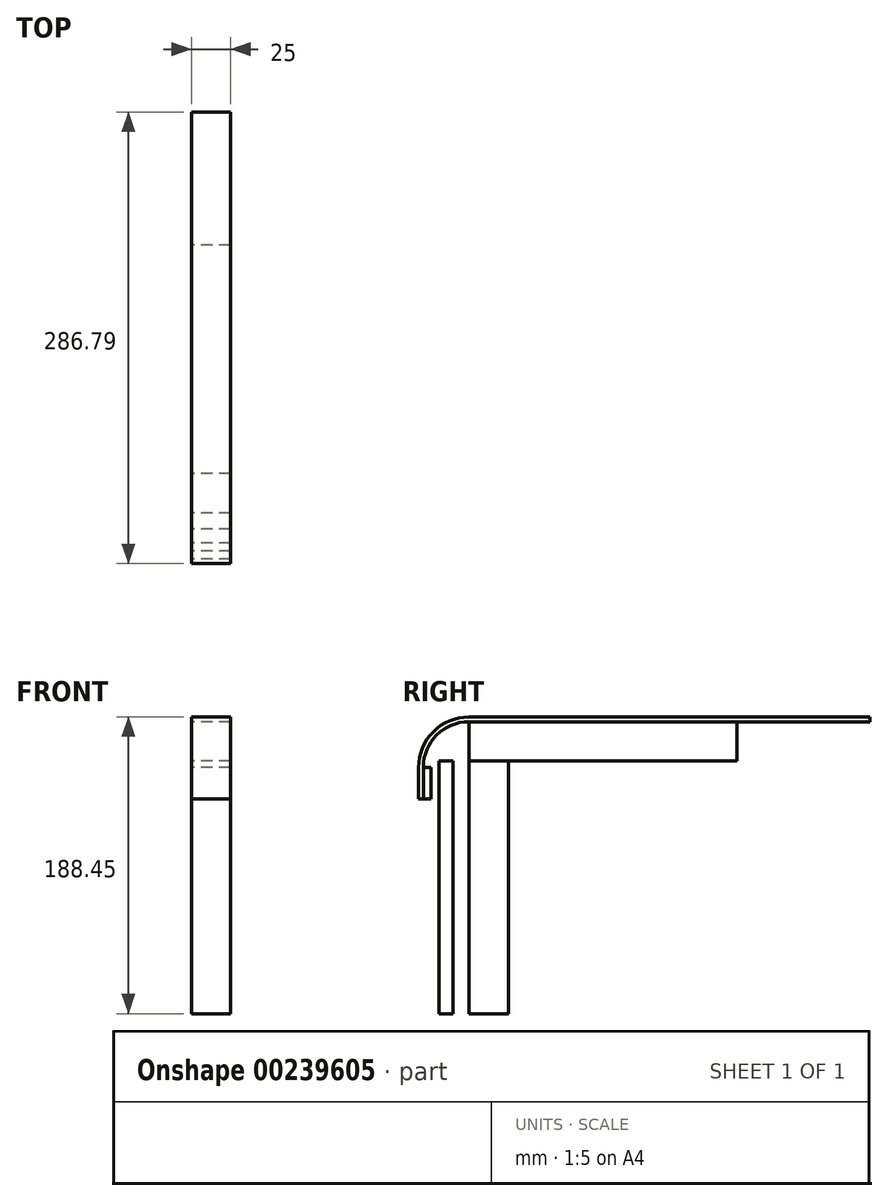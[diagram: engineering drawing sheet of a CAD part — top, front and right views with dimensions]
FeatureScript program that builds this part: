
annotation { "Feature Type Name" : "Feature", "Feature Type Description" : "" }
export const myFeature = defineFeature(function(context is Context, id is Id, definition is map)
    precondition{}
    {
        {
            var Q0;
            Q0=qCreatedBy(makeId("Right.planeOp"),FACE);
            var sketch = newSketch(context, id + "F0", { "sketchPlane" : qUnion([Q0])});
            skLineSegment(sketch, "E0.bottom", {"start": v(0, 0) * mm, "end": v(25, 0) * mm});
            skLineSegment(sketch, "E0.top", {"start": v(0, 160.45) * mm, "end": v(25, 160.45) * mm});
            skLineSegment(sketch, "E0.left", {"start": v(0, 0) * mm, "end": v(0, 160.45) * mm});
            skLineSegment(sketch, "E0.right", {"start": v(25, 0) * mm, "end": v(25, 160.45) * mm});
            skLineSegment(sketch, "E1.bottom", {"start": v(0, 160.45) * mm, "end": v(170.13, 160.45) * mm});
            skLineSegment(sketch, "E1.top", {"start": v(0, 185.45) * mm, "end": v(170.13, 185.45) * mm});
            skLineSegment(sketch, "E1.left", {"start": v(0, 160.45) * mm, "end": v(0, 185.45) * mm});
            skLineSegment(sketch, "E1.right", {"start": v(170.13, 160.45) * mm, "end": v(170.13, 185.45) * mm});
            skLineSegment(sketch, "E2", {"start": v(254.8, 188.45) * mm, "end": v(0, 188.45) * mm});
            skLineSegment(sketch, "E3.bottom", {"start": v(-10, 160.45) * mm, "end": v(-19, 160.45) * mm});
            skLineSegment(sketch, "E3.top", {"start": v(-10, 0) * mm, "end": v(-19, 0) * mm});
            skLineSegment(sketch, "E3.left", {"start": v(-10, 160.45) * mm, "end": v(-10, 0) * mm});
            skLineSegment(sketch, "E3.right", {"start": v(-19, 160.45) * mm, "end": v(-19, 0) * mm});
            skLineSegment(sketch, "E4.bottom", {"start": v(-29, 156.45) * mm, "end": v(-24, 156.45) * mm});
            skLineSegment(sketch, "E4.top", {"start": v(-29, 136.45) * mm, "end": v(-24, 136.45) * mm});
            skLineSegment(sketch, "E4.left", {"start": v(-29, 156.45) * mm, "end": v(-29, 136.45) * mm});
            skLineSegment(sketch, "E4.right", {"start": v(-24, 156.45) * mm, "end": v(-24, 136.45) * mm});
            skArc(sketch, "E5", {"start": v(0, 185.45) * mm, "mid": v(-20.5, 176.96) * mm, "end": v(-29, 156.45) * mm});
            skArc(sketch, "E6", {"start": v(0, 188.45) * mm, "mid": v(-22.63, 179.08) * mm, "end": v(-32, 156.45) * mm});
            skLineSegment(sketch, "E7", {"start": v(-32, 156.45) * mm, "end": v(-32, 136.45) * mm});
            skLineSegment(sketch, "E8", {"start": v(-32, 136.45) * mm, "end": v(-29, 136.45) * mm});
            skLineSegment(sketch, "E9", {"start": v(170.13, 185.45) * mm, "end": v(254.8, 185.45) * mm});
            skLineSegment(sketch, "E10", {"start": v(254.8, 185.45) * mm, "end": v(254.8, 188.45) * mm});
            skSolve(sketch);
        }
        {
            var Q0;
            Q0=makeQuery(id+"F0.imprint","IMPRINT",FACE,{"disambiguationData":[TD([[makeQuery(id+"F0.imprint","IMPRINT",EDGE,{"derivedFrom":sQuery(id+"F0.wireOp",EDGE,"E1.top")}),1.0]])]});
            extrude(context, id + "F1", {"entities" : qUnion([Q0]), "depth" : 25 * mm});
        }
        {
            var Q0;
            Q0=makeQuery(id+"F0.imprint","IMPRINT",FACE,{"disambiguationData":[TD([[makeQuery(id+"F0.imprint","IMPRINT",EDGE,{"derivedFrom":sQuery(id+"F0.wireOp",EDGE,"E1.top")}),-1.0]])]});
            extrude(context, id + "F2", {"entities" : qUnion([Q0]), "depth" : 25 * mm});
        }
        {
            var Q0;
            Q0=makeQuery(id+"F0.imprint","IMPRINT",FACE,{"disambiguationData":[TD([[makeQuery(id+"F0.imprint","IMPRINT",EDGE,{"derivedFrom":sQuery(id+"F0.wireOp",EDGE,"E0.bottom")}),1.0]])]});
            extrude(context, id + "F3", {"entities" : qUnion([Q0]), "depth" : 25 * mm});
        }
        {
            var Q0;
            Q0=makeQuery(id+"F0.imprint","IMPRINT",FACE,{"disambiguationData":[TD([[makeQuery(id+"F0.imprint","IMPRINT",EDGE,{"derivedFrom":sQuery(id+"F0.wireOp",EDGE,"E3.bottom")}),1.0]])]});
            extrude(context, id + "F4", {"entities" : qUnion([Q0]), "depth" : 25 * mm});
        }
        {
            var Q0;
            Q0=makeQuery(id+"F0.imprint","IMPRINT",FACE,{"disambiguationData":[TD([[makeQuery(id+"F0.imprint","IMPRINT",EDGE,{"derivedFrom":sQuery(id+"F0.wireOp",EDGE,"E4.bottom")}),-1.0]])]});
            extrude(context, id + "F5", {"entities" : qUnion([Q0]), "depth" : 25 * mm});
        }
    });
